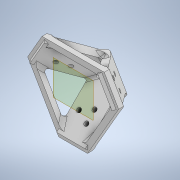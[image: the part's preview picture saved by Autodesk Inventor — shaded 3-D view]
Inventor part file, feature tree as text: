
AUTODESK INVENTOR PART (.ipt)
format: ipt  version: 2020 (Build 240168000, 168)  size: 491,520 bytes
history: native  units: mm
features: extrude x15, sketch x15, projected_geometry x11, reference x10, fillet x7, other x6, thicken_offset x3, pattern_circular x1, chamfer x1, plane x1
ambient origin geometry x8: Origin, YZ Plane, XZ Plane, XY Plane, X Axis, Y Axis, Z Axis, Center Point
bodies: Solid1 (feature_tree)
feature tree (70):
  extrude  "Extrusion1"  Depth=20.0mm
  extrude  "Extrusion2"  Depth=5.0mm
  extrude  "Extrusion3"  Depth=20.0mm
  extrude  "Extrusion4"  Depth=5.0mm
  extrude  "Extrusion5"  Depth=5.0mm
  extrude  "Extrusion6"  Depth=20.0mm
  extrude  "Extrusion7"  Depth=20.0mm TaperAngle=0.0deg
  pattern_circular  "Circular Pattern1"  Count=2  [1 undecoded]
  extrude  "Extrusion8"  Depth=35.0mm
  fillet  "Fillet1"  Radius=20.0mm
  fillet  "Fillet2"  Radius=20.0mm
  fillet  "Fillet3"  Radius=20.0mm
  chamfer  "Chamfer1"  Distance=5.0mm
  extrude  "Extrusion9"  Depth=5.0mm TaperAngle=0.0deg
  extrude  "Extrusion10"  Depth=1.0mm
  extrude  "Extrusion11"  Depth=3.0mm TaperAngle=45.0deg
  extrude  "Extrusion12"  Depth=5.0mm TaperAngle=0.0deg
  extrude  "Extrusion13"  Depth=3.0mm
  extrude  "Extrusion14"  Depth=1.0mm
  plane  "Work Plane1"
  extrude  "Extrusion15"  Depth=1.0mm TaperAngle=0.0deg
  thicken_offset  "Thicken1"
  thicken_offset  "Thicken2"
  thicken_offset  "Thicken3"
  fillet  "Fillet4"  Radius=3.0mm
  fillet  "Fillet5"  Radius=3.0mm
  fillet  "Fillet6"  Radius=3.0mm
  fillet  "Fillet7"  Radius=5.0mm
  sketch  "Sketch1"  dims[d0=20.0mm d1=20.0mm]
  sketch  "Sketch2"  dims[d2=60.0deg d3=5.0mm]
  projected_geometry  "Projected Loop1"
  sketch  "Sketch3"  dims[d4=20.0mm d5=20.0mm]
  projected_geometry  "Projected Loop2"
  sketch  "Sketch4"  dims[d6=5.0mm d7=5.0mm]
  projected_geometry  "Projected Loop3"
  sketch  "Sketch5"  dims[d8=20.0mm d9=5.0mm]
  projected_geometry  "Projected Loop4"
  sketch  "Sketch6"  dims[d10=3.0mm d11=0.0mm d12=20.0mm]
  projected_geometry  "Projected Loop5"
  sketch  "Sketch7"  dims[d13=20.0mm d14=20.0mm d15=0.0mm d16=20.0mm d17=0.0mm]
  sketch  "Sketch8"  dims[d18=5.0mm d19=35.0mm d20=20.0mm d21=0.0mm d22=20.0mm d23=0.0mm d24=20.0mm d25=0.0mm]
  sketch  "Sketch9"  dims[d26=3.0mm d27=5.0mm d28=0.0mm]
  projected_geometry  "Projected Loop6"
  sketch  "Sketch10"  dims[d29=30.0mm d30=360.0deg d32=5.0mm d33=0.0mm]
  projected_geometry  "Projected Loop7"
  sketch  "Sketch11"  dims[d34=1.0mm d35=2.0mm]
  projected_geometry  "Projected Loop8"
  sketch  "Sketch12"  dims[d36=2.0mm d37=3.0mm d38=2.0mm d39=45.0deg]
  reference  "Reference1"
  reference  "Reference2"
  reference  "Reference3"
  reference  "Reference4"
  sketch  "Sketch13"  dims[d40=5.0mm d41=0.0mm d42=5.0mm d43=0.0mm]
  reference  "Reference5"
  reference  "Reference6"
  reference  "Reference7"
  sketch  "Sketch14"  dims[d44=5.0mm d45=0.0mm d46=3.0mm]
  reference  "Reference8"
  reference  "Reference9"
  reference  "Reference10"
  sketch  "Sketch15"  dims[d47=3.0mm d48=3.0mm d49=5.0mm d50=0.0mm d51=3.0mm d52=3.0mm d53=3.0mm d54=5.0mm d55=0.0mm d56=3.0mm d57=3.0mm d58=3.0mm d59=5.0mm d60=0.0mm d61=-25.0mm d62=3.5mm d63=0.0mm d64=2.0mm d65=2.0mm d66=2.0mm d67=2.0mm d68=2.0mm d69=2.0mm d70=3.0mm d71=3.0mm d72=4.0mm d73=1.0mm]
  projected_geometry  "Projected Loop9"
  projected_geometry  "Projected Loop10"
  projected_geometry  "Projected Loop11"
  parser-record x1  (decoder bookkeeping rows leaked as tree rows — omitted from the tree; the rows remain in map.json)
  other  "delta_1.iam"
  other  "arm_shift_1:3"
  other  "motor_holder_1:1"
  other  "arm_shift_1:2"
  other  "arm_shift_1:1"
note: 1 required parameter value undecoded (feature->parameter linkage not recoverable at this tier; creation-order binding heuristic only, values carry confidence <= 0.55)
note: 1 file-system path scrubbed to <path> (originals preserved in map.json)
